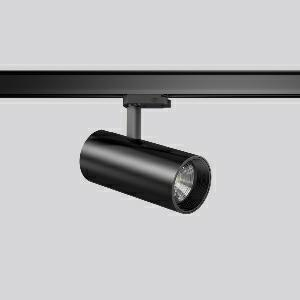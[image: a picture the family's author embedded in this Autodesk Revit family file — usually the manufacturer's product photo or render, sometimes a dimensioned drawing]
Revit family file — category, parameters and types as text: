
# Revit family: deecos_s_mini_742200_003_2_068f
name_source: partatom
category: Lighting Fixtures
units: mm (PartAtom-declared; Revit-internal decimal feet)

## family parameters
Cut with Voids When Loaded = No
Host = Face
Light Source = No
Part Type = Normal
Room Calculation Point = No
Round Connector Dimension = Use Diameter
Shared = No

## types (1)
- DEECOS S mini (1 x LED Modul 927, 1900 lm, 2700)
    Apparent Load = 20 VA
    Approval mark = CE
    CIE Flux Codes = 98 100 100 100 100
    Color Rendering = 92
    Color Temperature = 2700
    Default Elevation = 1800 mm
    Description = Series: DEECOS S mini
LED surface-mounted projector in modern design with no visible cooling ribs. Housing: die-cast aluminium, powder-coated. Rotation range: 356°. Swivel range: 90°. Black plastic ring and recessed LED to prevent glare from the side. Optical assembly with lens made of plastic (polycarbonate) for the best homogeneous light distribution - can be changed without tools. Best colour rendering index Ra>90. With multi adaptor for 3-circuit tracks 230 V. Suitable for Track on ceiling, Wall track. High quality converter without flickering and stroboscopic effect. The following accessories can be mounted without use of tools: interchangeable lenses, decorative glasses, honeycomb louvre, clear and frosted diffusers, white interchangeable plastic ring. 
Colour: deep black, matt (RAL 9005)
Diameter: 87 mm
Height: 214 mm
Lamp: LED
Socket: without socket
Colour temperature: 2700K
Colour rendering index (CRI): 92
System power: 20 W
Rated luminous flux: 1900 lm
Luminous efficiency: 95 lm/W
Control gear: Regulated power supply
Protection class: I
Type of protection: IP 20
    Height = 214 mm
    Lamp = 1 x LED Modul 927
    Lamp Light Flux = 1900 lm
    Lamp count = 1
    Length = 87 mm
    Lifetime = 50000 h
    Luminous efficacy = 95 lm/W
    Manufacturer = RZB
    ModVariant = No
    Model = 742200.003.2
    Mounting Place = Ceiling
    Mounting Type = Rail mounted
    Number of Poles = 1
    OnlyDefault = Yes
    Power Factor = 1
    Product Name = DEECOS S mini
    Product group = Track mounted projectors
    ProductGroupID = 301
    Protection Class = Protection class I
    Protection Degree = IP 20
    RLX_Detail_Level = 1
    RLX_Emergency_Light_Flux = 0 lm
    RLX_Emergency_Type = 0
    RLX_Emergency_Type_DB = No
    RlxData = <blob elided: 39097 chars, md5=16c06430>
    Socket = socket
    Standby Power = 0 W
    System Light Flux = 1900 lm
    System Power = 20 W
    Type Comments = Product without accessories
    Type Image = 741930.003.jpg
    URL = http://relux.com
    VarID = ---
    Voltage = 230 V
    Voltage Range = 220-240 V
    Weight = 0.00 kg
    Width = 0 mm  [stored 0 ft]

note: [stored X ft] marks values corroborated as IEEE doubles in the binary element streams (Revit-internal decimal feet)

## geometry (parser evidence)
native form markers: Blend x4, Sweep x13
no freeform markers — native parametric forms only
